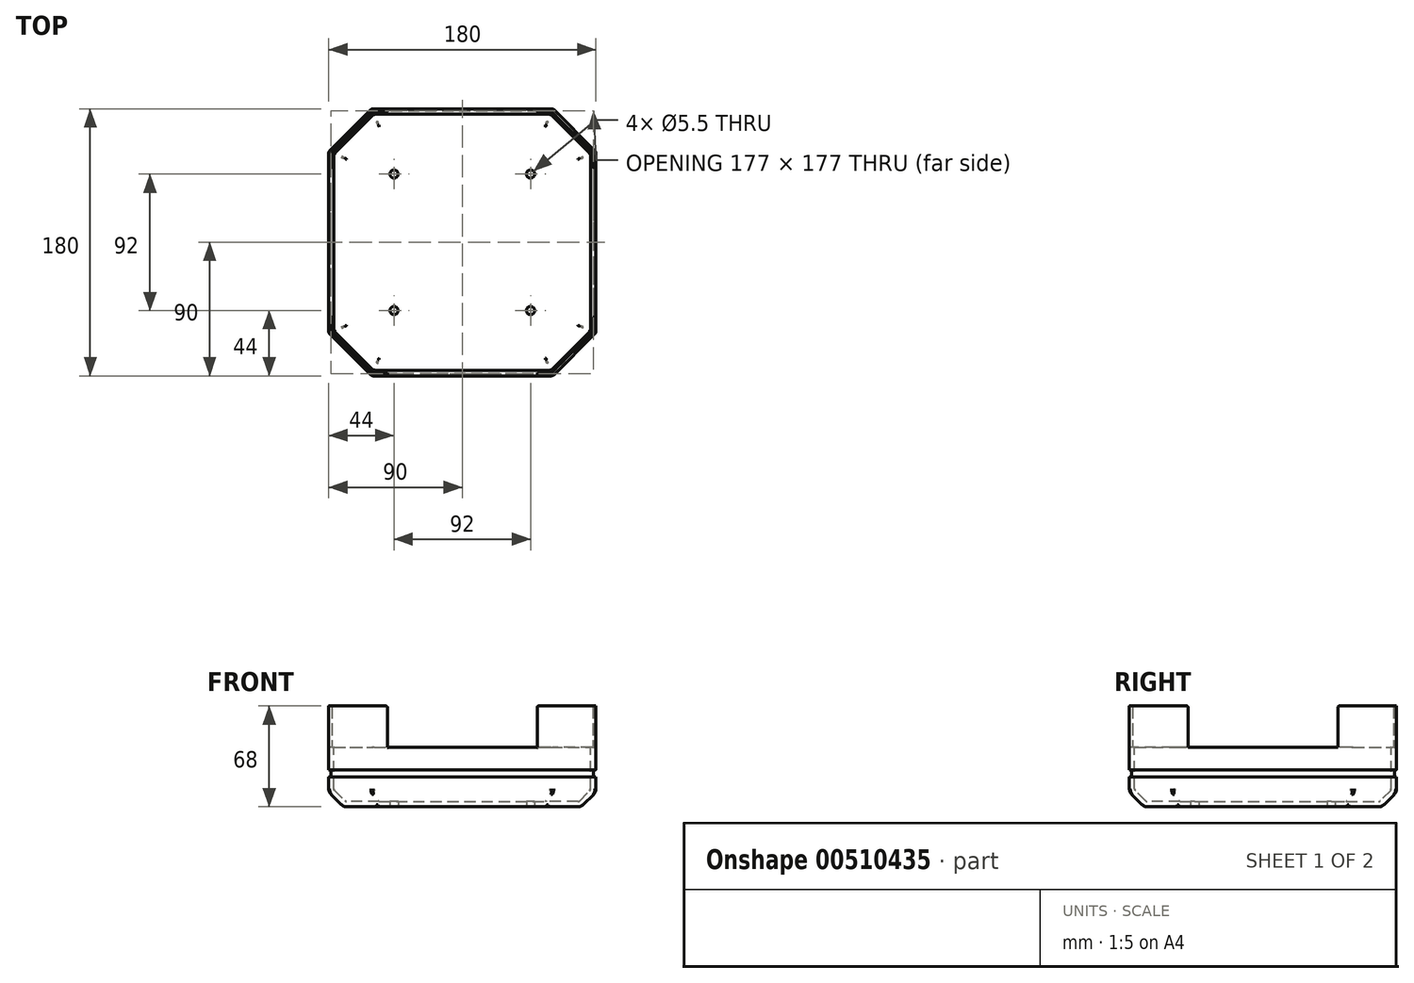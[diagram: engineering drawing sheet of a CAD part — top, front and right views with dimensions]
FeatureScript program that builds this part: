
annotation { "Feature Type Name" : "Feature", "Feature Type Description" : "" }
export const myFeature = defineFeature(function(context is Context, id is Id, definition is map)
    precondition{}
    {
        {
            var Q0;
            Q0=qCreatedBy(makeId("Top.planeOp"),FACE);
            var sketch = newSketch(context, id + "F0", { "sketchPlane" : qUnion([Q0])});
            skLineSegment(sketch, "E0.bottom", {"start": v(-61, 90) * mm, "end": v(61, 90) * mm});
            skLineSegment(sketch, "E0.top", {"start": v(-61, -90) * mm, "end": v(61, -90) * mm});
            skLineSegment(sketch, "E0.left", {"start": v(-90, 61) * mm, "end": v(-90, -61) * mm});
            skLineSegment(sketch, "E0.right", {"start": v(90, 61) * mm, "end": v(90, -61) * mm});
            skLineSegment(sketch, "E1", {"start": v(0, 156.9) * mm, "end": v(0, -146.72) * mm, "construction": true});
            skLineSegment(sketch, "E2", {"start": v(-149.43, 0) * mm, "end": v(169.81, 0) * mm, "construction": true});
            skLineSegment(sketch, "E3", {"start": v(-90, 61) * mm, "end": v(-61, 90) * mm});
            skLineSegment(sketch, "E4", {"start": v(-90, -61) * mm, "end": v(-61, -90) * mm});
            skLineSegment(sketch, "E5", {"start": v(61, -90) * mm, "end": v(90, -61) * mm});
            skLineSegment(sketch, "E6", {"start": v(61, 90) * mm, "end": v(90, 61) * mm});
            skPoint(sketch, "E7.orphan", {"position": v(-90, 90) * mm});
            skPoint(sketch, "E8.orphan", {"position": v(90, 90) * mm});
            skPoint(sketch, "E9.orphan", {"position": v(90, -90) * mm});
            skPoint(sketch, "E10.orphan", {"position": v(-90, -90) * mm});
            skSolve(sketch);
        }
        {
            var Q0;
            Q0=qSketchRegion(id+"F0",true);
            extrude(context, id + "F1", {"entities" : qUnion([Q0]), "depth" : 40 * mm});
        }
        {
            var Q0;
            Q0=makeQuery(id+"F1.opExtrude","CAP_EDGE",EDGE,{"disambiguationData":[OSD([sQuery(id+"F0.wireOp",EDGE,"E0.top")])],"isStart":true});
            var Q1;
            Q1=makeQuery(id+"F1.opExtrude","CAP_EDGE",EDGE,{"disambiguationData":[OSD([sQuery(id+"F0.wireOp",EDGE,"E4")])],"isStart":true});
            var Q2;
            Q2=makeQuery(id+"F1.opExtrude","CAP_EDGE",EDGE,{"disambiguationData":[OSD([sQuery(id+"F0.wireOp",EDGE,"E0.left")])],"isStart":true});
            var Q3;
            Q3=makeQuery(id+"F1.opExtrude","CAP_EDGE",EDGE,{"disambiguationData":[OSD([sQuery(id+"F0.wireOp",EDGE,"E3")])],"isStart":true});
            var Q4;
            Q4=makeQuery(id+"F1.opExtrude","CAP_EDGE",EDGE,{"disambiguationData":[OSD([sQuery(id+"F0.wireOp",EDGE,"E0.bottom")])],"isStart":true});
            var Q5;
            Q5=makeQuery(id+"F1.opExtrude","CAP_EDGE",EDGE,{"disambiguationData":[OSD([sQuery(id+"F0.wireOp",EDGE,"E6")])],"isStart":true});
            var Q6;
            Q6=makeQuery(id+"F1.opExtrude","CAP_EDGE",EDGE,{"disambiguationData":[OSD([sQuery(id+"F0.wireOp",EDGE,"E0.right")])],"isStart":true});
            var Q7;
            Q7=makeQuery(id+"F1.opExtrude","CAP_EDGE",EDGE,{"disambiguationData":[OSD([sQuery(id+"F0.wireOp",EDGE,"E5")])],"isStart":true});
            chamfer(context, id + "F2", {"entities" : qUnion([Q0, Q1, Q2, Q3, Q4, Q5, Q6, Q7]), "chamferType" : ChamferType.TWO_OFFSETS, "width1" : 10 * mm, "oppositeDirection" : true, "width2" : 10 * mm, "tangentPropagation" : true});
        }
        {
            var Q0;
            Q0=makeQuery(id+"F1.opExtrude","CAP_FACE",FACE,{"disambiguationData":[OSD([sQuery(id+"F0.wireOp",EDGE,"E0.bottom"),sQuery(id+"F0.wireOp",EDGE,"E0.top"),sQuery(id+"F0.wireOp",EDGE,"E0.left"),sQuery(id+"F0.wireOp",EDGE,"E0.right"),sQuery(id+"F0.wireOp",EDGE,"E3"),sQuery(id+"F0.wireOp",EDGE,"E4"),sQuery(id+"F0.wireOp",EDGE,"E5"),sQuery(id+"F0.wireOp",EDGE,"E6")])],"isStart":false});
            var sketch = newSketch(context, id + "F3", { "sketchPlane" : qUnion([Q0])});
            skLineSegment(sketch, "E11", {"start": v(90, -61) * mm, "end": v(61, -90) * mm});
            skLineSegment(sketch, "E12.0", {"start": v(88, -60.17) * mm, "end": v(60.17, -88) * mm});
            skLineSegment(sketch, "E13", {"start": v(90, -61) * mm, "end": v(90, -90) * mm, "construction": true});
            skLineSegment(sketch, "E14", {"start": v(90, -90) * mm, "end": v(61, -90) * mm, "construction": true});
            skLineSegment(sketch, "E15", {"start": v(90, -61) * mm, "end": v(90, -50.5) * mm});
            skLineSegment(sketch, "E16", {"start": v(61, -90) * mm, "end": v(50.5, -90) * mm});
            skLineSegment(sketch, "E17.0", {"start": v(60.17, -88) * mm, "end": v(50.5, -88) * mm});
            skLineSegment(sketch, "E18.0", {"start": v(88, -60.17) * mm, "end": v(88, -50.5) * mm});
            skLineSegment(sketch, "E19", {"start": v(88, -50.5) * mm, "end": v(90, -50.5) * mm});
            skLineSegment(sketch, "E20", {"start": v(50.5, -88) * mm, "end": v(50.5, -90) * mm});
            skLineSegment(sketch, "E21", {"start": v(104.54, 0) * mm, "end": v(-130.04, 0) * mm, "construction": true});
            skPoint(sketch, "E21.endSnap0", {"position": v(-90, 0) * mm});
            skLineSegment(sketch, "E22", {"start": v(0, 121.87) * mm, "end": v(0, -139.26) * mm, "construction": true});
            skLineSegment(sketch, "E23.MirrorCS", {"start": v(88, 50.5) * mm, "end": v(90, 50.5) * mm});
            skLineSegment(sketch, "E24.MirrorCS", {"start": v(50.5, 88) * mm, "end": v(50.5, 90) * mm});
            skLineSegment(sketch, "E25.MirrorCS", {"start": v(61, 90) * mm, "end": v(50.5, 90) * mm});
            skLineSegment(sketch, "E26.MirrorCS", {"start": v(60.17, 88) * mm, "end": v(50.5, 88) * mm});
            skLineSegment(sketch, "E27.MirrorCS", {"start": v(88, 60.17) * mm, "end": v(88, 50.5) * mm});
            skLineSegment(sketch, "E28.MirrorCS", {"start": v(90, 61) * mm, "end": v(90, 50.5) * mm});
            skLineSegment(sketch, "E29.MirrorCS", {"start": v(90, 61) * mm, "end": v(61, 90) * mm});
            skLineSegment(sketch, "E30.MirrorCS", {"start": v(88, 60.17) * mm, "end": v(60.17, 88) * mm});
            skLineSegment(sketch, "E31.MirrorCS", {"start": v(90, 90) * mm, "end": v(61, 90) * mm, "construction": true});
            skLineSegment(sketch, "E32.MirrorCS", {"start": v(90, 61) * mm, "end": v(90, 90) * mm, "construction": true});
            skLineSegment(sketch, "E33.MirrorCS", {"start": v(-88, 50.5) * mm, "end": v(-90, 50.5) * mm});
            skLineSegment(sketch, "E34.MirrorCS", {"start": v(-50.5, 88) * mm, "end": v(-50.5, 90) * mm});
            skLineSegment(sketch, "E35.MirrorCS", {"start": v(-88, -50.5) * mm, "end": v(-90, -50.5) * mm});
            skLineSegment(sketch, "E36.MirrorCS", {"start": v(-50.5, -88) * mm, "end": v(-50.5, -90) * mm});
            skLineSegment(sketch, "E37.MirrorCS", {"start": v(-61, -90) * mm, "end": v(-50.5, -90) * mm});
            skLineSegment(sketch, "E38.MirrorCS", {"start": v(-88, 60.17) * mm, "end": v(-88, 50.5) * mm});
            skLineSegment(sketch, "E39.MirrorCS", {"start": v(-61, 90) * mm, "end": v(-50.5, 90) * mm});
            skLineSegment(sketch, "E40.MirrorCS", {"start": v(-88, 60.17) * mm, "end": v(-60.17, 88) * mm});
            skLineSegment(sketch, "E41.MirrorCS", {"start": v(-88, -60.17) * mm, "end": v(-88, -50.5) * mm});
            skLineSegment(sketch, "E42.MirrorCS", {"start": v(-90, 61) * mm, "end": v(-61, 90) * mm});
            skLineSegment(sketch, "E43.MirrorCS", {"start": v(-60.17, 88) * mm, "end": v(-50.5, 88) * mm});
            skLineSegment(sketch, "E44.MirrorCS", {"start": v(-90, 61) * mm, "end": v(-90, 50.5) * mm});
            skLineSegment(sketch, "E45.MirrorCS", {"start": v(-90, -61) * mm, "end": v(-90, -50.5) * mm});
            skLineSegment(sketch, "E46.MirrorCS", {"start": v(-60.17, -88) * mm, "end": v(-50.5, -88) * mm});
            skLineSegment(sketch, "E47.MirrorCS", {"start": v(-90, 90) * mm, "end": v(-61, 90) * mm, "construction": true});
            skLineSegment(sketch, "E48.MirrorCS", {"start": v(-90, 61) * mm, "end": v(-90, 90) * mm, "construction": true});
            skLineSegment(sketch, "E49.MirrorCS", {"start": v(-90, -61) * mm, "end": v(-61, -90) * mm});
            skLineSegment(sketch, "E50.MirrorCS", {"start": v(-90, -61) * mm, "end": v(-90, -90) * mm, "construction": true});
            skLineSegment(sketch, "E51.MirrorCS", {"start": v(-90, -90) * mm, "end": v(-61, -90) * mm, "construction": true});
            skLineSegment(sketch, "E52.MirrorCS", {"start": v(-88, -60.17) * mm, "end": v(-60.17, -88) * mm});
            skSolve(sketch);
        }
        {
            var Q0;
            Q0=qSketchRegion(id+"F3",true);
            extrude(context, id + "F4", {"entities" : qUnion([Q0]), "operationType" : NewBodyOperationType.ADD, "depth" : 28 * mm});
        }
        {
            var Q0;
            {var subQ0=sQuery(id+"F0.wireOp",EDGE,"E6");Q0=makeQuery(id+"F2.opChamfer","BLEND_EDGE",EDGE,{"blendedFrom":[makeQuery(id+"F1.opExtrude","CAP_EDGE",EDGE,{"disambiguationData":[OSD([subQ0])],"isStart":true}),makeQuery(id+"F1.opExtrude","SWEPT_FACE",FACE,{"disambiguationData":[OSD([subQ0])]})],"blendedInto":[makeQuery(id+"F1.opExtrude","SWEPT_FACE",FACE,{"disambiguationData":[OSD([subQ0])]})]});}
            var Q1;
            {var subQ0=sQuery(id+"F0.wireOp",EDGE,"E0.right");Q1=makeQuery(id+"F2.opChamfer","BLEND_EDGE",EDGE,{"blendedFrom":[makeQuery(id+"F1.opExtrude","CAP_EDGE",EDGE,{"disambiguationData":[OSD([subQ0])],"isStart":true}),makeQuery(id+"F1.opExtrude","SWEPT_FACE",FACE,{"disambiguationData":[OSD([subQ0])]})],"blendedInto":[makeQuery(id+"F1.opExtrude","SWEPT_FACE",FACE,{"disambiguationData":[OSD([subQ0])]})]});}
            var Q2;
            {var subQ0=sQuery(id+"F0.wireOp",EDGE,"E5");Q2=makeQuery(id+"F2.opChamfer","BLEND_EDGE",EDGE,{"blendedFrom":[makeQuery(id+"F1.opExtrude","CAP_EDGE",EDGE,{"disambiguationData":[OSD([subQ0])],"isStart":true}),makeQuery(id+"F1.opExtrude","SWEPT_FACE",FACE,{"disambiguationData":[OSD([subQ0])]})],"blendedInto":[makeQuery(id+"F1.opExtrude","SWEPT_FACE",FACE,{"disambiguationData":[OSD([subQ0])]})]});}
            var Q3;
            {var subQ0=sQuery(id+"F0.wireOp",EDGE,"E0.top");Q3=makeQuery(id+"F2.opChamfer","BLEND_EDGE",EDGE,{"blendedFrom":[makeQuery(id+"F1.opExtrude","CAP_EDGE",EDGE,{"disambiguationData":[OSD([subQ0])],"isStart":true}),makeQuery(id+"F1.opExtrude","SWEPT_FACE",FACE,{"disambiguationData":[OSD([subQ0])]})],"blendedInto":[makeQuery(id+"F1.opExtrude","SWEPT_FACE",FACE,{"disambiguationData":[OSD([subQ0])]})]});}
            var Q4;
            {var subQ0=sQuery(id+"F0.wireOp",EDGE,"E4");Q4=makeQuery(id+"F2.opChamfer","BLEND_EDGE",EDGE,{"blendedFrom":[makeQuery(id+"F1.opExtrude","CAP_EDGE",EDGE,{"disambiguationData":[OSD([subQ0])],"isStart":true}),makeQuery(id+"F1.opExtrude","SWEPT_FACE",FACE,{"disambiguationData":[OSD([subQ0])]})],"blendedInto":[makeQuery(id+"F1.opExtrude","SWEPT_FACE",FACE,{"disambiguationData":[OSD([subQ0])]})]});}
            var Q5;
            {var subQ0=sQuery(id+"F0.wireOp",EDGE,"E0.left");Q5=makeQuery(id+"F2.opChamfer","BLEND_EDGE",EDGE,{"blendedFrom":[makeQuery(id+"F1.opExtrude","CAP_EDGE",EDGE,{"disambiguationData":[OSD([subQ0])],"isStart":true}),makeQuery(id+"F1.opExtrude","SWEPT_FACE",FACE,{"disambiguationData":[OSD([subQ0])]})],"blendedInto":[makeQuery(id+"F1.opExtrude","SWEPT_FACE",FACE,{"disambiguationData":[OSD([subQ0])]})]});}
            var Q6;
            {var subQ0=sQuery(id+"F0.wireOp",EDGE,"E3");Q6=makeQuery(id+"F2.opChamfer","BLEND_EDGE",EDGE,{"blendedFrom":[makeQuery(id+"F1.opExtrude","CAP_EDGE",EDGE,{"disambiguationData":[OSD([subQ0])],"isStart":true}),makeQuery(id+"F1.opExtrude","SWEPT_FACE",FACE,{"disambiguationData":[OSD([subQ0])]})],"blendedInto":[makeQuery(id+"F1.opExtrude","SWEPT_FACE",FACE,{"disambiguationData":[OSD([subQ0])]})]});}
            var Q7;
            {var subQ0=sQuery(id+"F0.wireOp",EDGE,"E0.bottom");Q7=makeQuery(id+"F2.opChamfer","BLEND_EDGE",EDGE,{"blendedFrom":[makeQuery(id+"F1.opExtrude","CAP_EDGE",EDGE,{"disambiguationData":[OSD([subQ0])],"isStart":true}),makeQuery(id+"F1.opExtrude","SWEPT_FACE",FACE,{"disambiguationData":[OSD([subQ0])]})],"blendedInto":[makeQuery(id+"F1.opExtrude","SWEPT_FACE",FACE,{"disambiguationData":[OSD([subQ0])]})]});}
            fillet(context, id + "F5", {"entities" : qUnion([Q0, Q1, Q2, Q3, Q4, Q5, Q6, Q7]), "radius" : 5 * mm, "tangentPropagation" : true, "allowEdgeOverflow" : false});
        }
        {
            var Q0;
            Q0=makeQuery(id+"F4.boolean.opBoolean","MERGE",EDGE,{"derivedFrom":[makeQuery(id+"F1.opExtrude","SWEPT_EDGE",EDGE,{"disambiguationData":[OSD([sQuery(id+"F0.wireOp",EDGE,"E0.bottom"),sQuery(id+"F0.wireOp",EDGE,"E6")])]}),makeQuery(id+"F4.opExtrude","SWEPT_EDGE",EDGE,{"disambiguationData":[OSD([sQuery(id+"F3.wireOp",EDGE,"E25.MirrorCS"),sQuery(id+"F3.wireOp",EDGE,"E29.MirrorCS")])]})]});
            var Q1;
            Q1=makeQuery(id+"F4.boolean.opBoolean","MERGE",EDGE,{"derivedFrom":[makeQuery(id+"F1.opExtrude","SWEPT_EDGE",EDGE,{"disambiguationData":[OSD([sQuery(id+"F0.wireOp",EDGE,"E0.right"),sQuery(id+"F0.wireOp",EDGE,"E6")])]}),makeQuery(id+"F4.opExtrude","SWEPT_EDGE",EDGE,{"disambiguationData":[OSD([sQuery(id+"F3.wireOp",EDGE,"E28.MirrorCS"),sQuery(id+"F3.wireOp",EDGE,"E29.MirrorCS")])]})]});
            var Q2;
            Q2=makeQuery(id+"F4.boolean.opBoolean","MERGE",EDGE,{"derivedFrom":[makeQuery(id+"F1.opExtrude","SWEPT_EDGE",EDGE,{"disambiguationData":[OSD([sQuery(id+"F0.wireOp",EDGE,"E0.bottom"),sQuery(id+"F0.wireOp",EDGE,"E3")])]}),makeQuery(id+"F4.opExtrude","SWEPT_EDGE",EDGE,{"disambiguationData":[OSD([sQuery(id+"F3.wireOp",EDGE,"E39.MirrorCS"),sQuery(id+"F3.wireOp",EDGE,"E42.MirrorCS")])]})]});
            var Q3;
            Q3=makeQuery(id+"F4.boolean.opBoolean","MERGE",EDGE,{"derivedFrom":[makeQuery(id+"F1.opExtrude","SWEPT_EDGE",EDGE,{"disambiguationData":[OSD([sQuery(id+"F0.wireOp",EDGE,"E0.right"),sQuery(id+"F0.wireOp",EDGE,"E5")])]}),makeQuery(id+"F4.opExtrude","SWEPT_EDGE",EDGE,{"disambiguationData":[OSD([sQuery(id+"F3.wireOp",EDGE,"E11"),sQuery(id+"F3.wireOp",EDGE,"E15")])]})]});
            var Q4;
            Q4=makeQuery(id+"F2.opChamfer","BLEND_EDGE",EDGE,{"blendedFrom":[makeQuery(id+"F1.opExtrude","CAP_EDGE",EDGE,{"disambiguationData":[OSD([sQuery(id+"F0.wireOp",EDGE,"E0.top")])],"isStart":true}),makeQuery(id+"F1.opExtrude","CAP_EDGE",EDGE,{"disambiguationData":[OSD([sQuery(id+"F0.wireOp",EDGE,"E5")])],"isStart":true})],"blendedInto":[]});
            var Q5;
            Q5=makeQuery(id+"F2.opChamfer","BLEND_EDGE",EDGE,{"blendedFrom":[makeQuery(id+"F1.opExtrude","CAP_EDGE",EDGE,{"disambiguationData":[OSD([sQuery(id+"F0.wireOp",EDGE,"E0.top")])],"isStart":true}),makeQuery(id+"F1.opExtrude","CAP_EDGE",EDGE,{"disambiguationData":[OSD([sQuery(id+"F0.wireOp",EDGE,"E4")])],"isStart":true})],"blendedInto":[]});
            var Q6;
            Q6=makeQuery(id+"F2.opChamfer","BLEND_EDGE",EDGE,{"blendedFrom":[makeQuery(id+"F1.opExtrude","CAP_EDGE",EDGE,{"disambiguationData":[OSD([sQuery(id+"F0.wireOp",EDGE,"E0.left")])],"isStart":true}),makeQuery(id+"F1.opExtrude","CAP_EDGE",EDGE,{"disambiguationData":[OSD([sQuery(id+"F0.wireOp",EDGE,"E4")])],"isStart":true})],"blendedInto":[]});
            var Q7;
            Q7=makeQuery(id+"F2.opChamfer","BLEND_EDGE",EDGE,{"blendedFrom":[makeQuery(id+"F1.opExtrude","CAP_EDGE",EDGE,{"disambiguationData":[OSD([sQuery(id+"F0.wireOp",EDGE,"E0.left")])],"isStart":true}),makeQuery(id+"F1.opExtrude","CAP_EDGE",EDGE,{"disambiguationData":[OSD([sQuery(id+"F0.wireOp",EDGE,"E3")])],"isStart":true})],"blendedInto":[]});
            fillet(context, id + "F6", {"entities" : qUnion([Q0, Q1, Q2, Q3, Q4, Q5, Q6, Q7]), "radius" : 2 * mm, "tangentPropagation" : true, "allowEdgeOverflow" : false});
        }
        {
            var Q0;
            {var subQ0=sQuery(id+"F0.wireOp",EDGE,"E0.left");Q0=makeQuery(id+"F2.opChamfer","BLEND_EDGE",EDGE,{"blendedFrom":[makeQuery(id+"F1.opExtrude","CAP_EDGE",EDGE,{"disambiguationData":[OSD([subQ0])],"isStart":true}),makeQuery(id+"F1.opExtrude","CAP_FACE",FACE,{"disambiguationData":[OSD([sQuery(id+"F0.wireOp",EDGE,"E0.bottom"),sQuery(id+"F0.wireOp",EDGE,"E0.top"),subQ0,sQuery(id+"F0.wireOp",EDGE,"E0.right"),sQuery(id+"F0.wireOp",EDGE,"E3"),sQuery(id+"F0.wireOp",EDGE,"E4"),sQuery(id+"F0.wireOp",EDGE,"E5"),sQuery(id+"F0.wireOp",EDGE,"E6")])],"isStart":true})],"blendedInto":[makeQuery(id+"F1.opExtrude","CAP_FACE",FACE,{"disambiguationData":[OSD([sQuery(id+"F0.wireOp",EDGE,"E0.bottom"),sQuery(id+"F0.wireOp",EDGE,"E0.top"),subQ0,sQuery(id+"F0.wireOp",EDGE,"E0.right"),sQuery(id+"F0.wireOp",EDGE,"E3"),sQuery(id+"F0.wireOp",EDGE,"E4"),sQuery(id+"F0.wireOp",EDGE,"E5"),sQuery(id+"F0.wireOp",EDGE,"E6")])],"isStart":true})]});}
            fillet(context, id + "F7", {"entities" : qUnion([Q0]), "radius" : 5 * mm, "tangentPropagation" : true, "allowEdgeOverflow" : false});
        }
        {
            var Q0;
            Q0=makeQuery(id+"F1.opExtrude","CAP_FACE",FACE,{"disambiguationData":[OSD([sQuery(id+"F0.wireOp",EDGE,"E0.bottom"),sQuery(id+"F0.wireOp",EDGE,"E0.top"),sQuery(id+"F0.wireOp",EDGE,"E0.left"),sQuery(id+"F0.wireOp",EDGE,"E0.right"),sQuery(id+"F0.wireOp",EDGE,"E3"),sQuery(id+"F0.wireOp",EDGE,"E4"),sQuery(id+"F0.wireOp",EDGE,"E5"),sQuery(id+"F0.wireOp",EDGE,"E6")])],"isStart":false});
            shell(context, id + "F8", {"entities" : qUnion([Q0]), "thickness" : 3.5 * mm});
        }
        {
            var Q0;
            Q0=qCreatedBy(makeId("Front.planeOp"),FACE);
            var sketch = newSketch(context, id + "F9", { "sketchPlane" : qUnion([Q0])});
            skLineSegment(sketch, "E53.bottom", {"start": v(124, 20) * mm, "end": v(-129.94, 20) * mm});
            skLineSegment(sketch, "E53.top", {"start": v(124, 25) * mm, "end": v(-129.94, 25) * mm});
            skLineSegment(sketch, "E53.left", {"start": v(124, 20) * mm, "end": v(124, 25) * mm});
            skLineSegment(sketch, "E53.right", {"start": v(-129.94, 20) * mm, "end": v(-129.94, 25) * mm});
            skSolve(sketch);
        }
        {
            var Q0;
            Q0=qSketchRegion(id+"F9",true);
            extrude(context, id + "F10", {"entities" : qUnion([Q0]), "operationType" : NewBodyOperationType.REMOVE, "oppositeDirection" : true, "depth" : 180 * mm, "symmetric" : true});
        }
        {
            var Q0;
            Q0=makeQuery(id+"F10.boolean.opBoolean","COPY",FACE,{"derivedFrom":makeQuery(id+"F10.opExtrude","SWEPT_FACE",FACE,{"disambiguationData":[OSD([sQuery(id+"F9.wireOp",EDGE,"E53.bottom")])]})});
            var sketch = newSketch(context, id + "F11", { "sketchPlane" : qUnion([Q0])});
            skLineSegment(sketch, "E54.0", {"start": v(-60.38, -88.5) * mm, "end": v(60.38, -88.5) * mm});
            skLineSegment(sketch, "E54.1", {"start": v(-88.5, -60.38) * mm, "end": v(-60.38, -88.5) * mm});
            skLineSegment(sketch, "E54.2", {"start": v(60.38, -88.5) * mm, "end": v(88.5, -60.38) * mm});
            skLineSegment(sketch, "E54.3", {"start": v(-88.5, 60.38) * mm, "end": v(-88.5, -60.38) * mm});
            skLineSegment(sketch, "E54.4", {"start": v(88.5, -60.38) * mm, "end": v(88.5, 60.38) * mm});
            skLineSegment(sketch, "E54.5", {"start": v(88.5, 60.38) * mm, "end": v(60.38, 88.5) * mm});
            skLineSegment(sketch, "E54.6", {"start": v(60.38, 88.5) * mm, "end": v(-60.38, 88.5) * mm});
            skLineSegment(sketch, "E54.7", {"start": v(-60.38, 88.5) * mm, "end": v(-88.5, 60.38) * mm});
            skLineSegment(sketch, "E55.0", {"start": v(-59.55, 86.5) * mm, "end": v(-59.55, 86.5) * mm});
            skLineSegment(sketch, "E55.2", {"start": v(-86.5, 59.55) * mm, "end": v(-86.5, -59.55) * mm});
            skLineSegment(sketch, "E55.4", {"start": v(-59.55, 86.5) * mm, "end": v(59.55, 86.5) * mm});
            skLineSegment(sketch, "E55.6", {"start": v(59.55, 86.5) * mm, "end": v(59.55, 86.5) * mm});
            skLineSegment(sketch, "E55.8", {"start": v(86.5, 59.55) * mm, "end": v(86.5, -59.55) * mm});
            skLineSegment(sketch, "E55.10", {"start": v(59.55, -86.5) * mm, "end": v(59.55, -86.5) * mm});
            skLineSegment(sketch, "E55.12", {"start": v(-59.55, -86.5) * mm, "end": v(59.55, -86.5) * mm});
            skLineSegment(sketch, "E55.14", {"start": v(-59.55, -86.5) * mm, "end": v(-59.55, -86.5) * mm});
            skLineSegment(sketch, "E56", {"start": v(86.5, 59.55) * mm, "end": v(59.55, 86.5) * mm});
            skLineSegment(sketch, "E57", {"start": v(-59.55, 86.5) * mm, "end": v(-86.5, 59.55) * mm});
            skLineSegment(sketch, "E58", {"start": v(-59.55, -86.5) * mm, "end": v(-86.5, -59.55) * mm});
            skLineSegment(sketch, "E59", {"start": v(86.5, -59.55) * mm, "end": v(59.55, -86.5) * mm});
            skSolve(sketch);
        }
        {
            var Q0;
            Q0=qSketchRegion(id+"F11",true);
            extrude(context, id + "F12", {"entities" : qUnion([Q0]), "operationType" : NewBodyOperationType.ADD, "depth" : 10 * mm});
        }
        {
            var Q0;
            {var subQ0=sQuery(id+"F11.wireOp",EDGE,"E54.7");var subQ1=sQuery(id+"F11.wireOp",EDGE,"E54.3");Q0=makeQuery(id+"F12.boolean.opBoolean","SPLIT",EDGE,{"disambiguationData":[TD([makeQuery(id+"F10.boolean.opBoolean","COPY",FACE,{"derivedFrom":makeQuery(id+"F10.opExtrude","SWEPT_FACE",FACE,{"disambiguationData":[OSD([sQuery(id+"F9.wireOp",EDGE,"E53.bottom")])]})})])],"derivedFrom":makeQuery(id+"F12.opExtrude","SWEPT_EDGE",EDGE,{"disambiguationData":[OSD([subQ1,subQ0])]})});}
            var Q1;
            {var subQ0=sQuery(id+"F11.wireOp",EDGE,"E54.7");var subQ1=sQuery(id+"F11.wireOp",EDGE,"E54.6");Q1=makeQuery(id+"F12.boolean.opBoolean","SPLIT",EDGE,{"disambiguationData":[TD([makeQuery(id+"F10.boolean.opBoolean","COPY",FACE,{"derivedFrom":makeQuery(id+"F10.opExtrude","SWEPT_FACE",FACE,{"disambiguationData":[OSD([sQuery(id+"F9.wireOp",EDGE,"E53.bottom")])]})})])],"derivedFrom":makeQuery(id+"F12.opExtrude","SWEPT_EDGE",EDGE,{"disambiguationData":[OSD([subQ1,subQ0])]})});}
            var Q2;
            {var subQ0=sQuery(id+"F11.wireOp",EDGE,"E54.5");var subQ1=sQuery(id+"F11.wireOp",EDGE,"E54.6");Q2=makeQuery(id+"F12.boolean.opBoolean","SPLIT",EDGE,{"disambiguationData":[TD([makeQuery(id+"F10.boolean.opBoolean","COPY",FACE,{"derivedFrom":makeQuery(id+"F10.opExtrude","SWEPT_FACE",FACE,{"disambiguationData":[OSD([sQuery(id+"F9.wireOp",EDGE,"E53.bottom")])]})})])],"derivedFrom":makeQuery(id+"F12.opExtrude","SWEPT_EDGE",EDGE,{"disambiguationData":[OSD([subQ0,subQ1])]})});}
            var Q3;
            {var subQ0=sQuery(id+"F11.wireOp",EDGE,"E54.5");var subQ1=sQuery(id+"F11.wireOp",EDGE,"E54.6");Q3=makeQuery(id+"F12.boolean.opBoolean","SPLIT",EDGE,{"disambiguationData":[TD([makeQuery(id+"F10.boolean.opBoolean","COPY",FACE,{"derivedFrom":makeQuery(id+"F10.opExtrude","SWEPT_FACE",FACE,{"disambiguationData":[OSD([sQuery(id+"F9.wireOp",EDGE,"Me13D1SK-nVIm-EUZ4-u9ei-o20qw3bNrjn4.bottom")])]})})])],"derivedFrom":makeQuery(id+"F12.opExtrude","SWEPT_EDGE",EDGE,{"disambiguationData":[OSD([subQ0,subQ1])]})});}
            var Q4;
            {var subQ0=sQuery(id+"F11.wireOp",EDGE,"E54.6");var subQ1=sQuery(id+"F11.wireOp",EDGE,"E54.7");Q4=makeQuery(id+"F12.boolean.opBoolean","SPLIT",EDGE,{"disambiguationData":[TD([makeQuery(id+"F10.boolean.opBoolean","COPY",FACE,{"derivedFrom":makeQuery(id+"F10.opExtrude","SWEPT_FACE",FACE,{"disambiguationData":[OSD([sQuery(id+"F9.wireOp",EDGE,"Me13D1SK-nVIm-EUZ4-u9ei-o20qw3bNrjn4.bottom")])]})})])],"derivedFrom":makeQuery(id+"F12.opExtrude","SWEPT_EDGE",EDGE,{"disambiguationData":[OSD([subQ0,subQ1])]})});}
            var Q5;
            {var subQ0=sQuery(id+"F11.wireOp",EDGE,"E54.3");var subQ1=sQuery(id+"F11.wireOp",EDGE,"E54.7");Q5=makeQuery(id+"F12.boolean.opBoolean","SPLIT",EDGE,{"disambiguationData":[TD([makeQuery(id+"F10.boolean.opBoolean","COPY",FACE,{"derivedFrom":makeQuery(id+"F10.opExtrude","SWEPT_FACE",FACE,{"disambiguationData":[OSD([sQuery(id+"F9.wireOp",EDGE,"Me13D1SK-nVIm-EUZ4-u9ei-o20qw3bNrjn4.bottom")])]})})])],"derivedFrom":makeQuery(id+"F12.opExtrude","SWEPT_EDGE",EDGE,{"disambiguationData":[OSD([subQ0,subQ1])]})});}
            var Q6;
            {var subQ0=sQuery(id+"F11.wireOp",EDGE,"E54.5");var subQ1=sQuery(id+"F11.wireOp",EDGE,"E54.4");Q6=makeQuery(id+"F12.boolean.opBoolean","SPLIT",EDGE,{"disambiguationData":[TD([makeQuery(id+"F10.boolean.opBoolean","COPY",FACE,{"derivedFrom":makeQuery(id+"F10.opExtrude","SWEPT_FACE",FACE,{"disambiguationData":[OSD([sQuery(id+"F9.wireOp",EDGE,"Me13D1SK-nVIm-EUZ4-u9ei-o20qw3bNrjn4.bottom")])]})})])],"derivedFrom":makeQuery(id+"F12.opExtrude","SWEPT_EDGE",EDGE,{"disambiguationData":[OSD([subQ1,subQ0])]})});}
            var Q7;
            {var subQ0=sQuery(id+"F11.wireOp",EDGE,"E54.4");var subQ1=sQuery(id+"F11.wireOp",EDGE,"E54.5");Q7=makeQuery(id+"F12.boolean.opBoolean","SPLIT",EDGE,{"disambiguationData":[TD([makeQuery(id+"F10.boolean.opBoolean","COPY",FACE,{"derivedFrom":makeQuery(id+"F10.opExtrude","SWEPT_FACE",FACE,{"disambiguationData":[OSD([sQuery(id+"F9.wireOp",EDGE,"E53.bottom")])]})})])],"derivedFrom":makeQuery(id+"F12.opExtrude","SWEPT_EDGE",EDGE,{"disambiguationData":[OSD([subQ0,subQ1])]})});}
            var Q8;
            {var subQ0=sQuery(id+"F11.wireOp",EDGE,"E54.2");var subQ1=sQuery(id+"F11.wireOp",EDGE,"E54.4");Q8=makeQuery(id+"F12.boolean.opBoolean","SPLIT",EDGE,{"disambiguationData":[TD([makeQuery(id+"F10.boolean.opBoolean","COPY",FACE,{"derivedFrom":makeQuery(id+"F10.opExtrude","SWEPT_FACE",FACE,{"disambiguationData":[OSD([sQuery(id+"F9.wireOp",EDGE,"E53.bottom")])]})})])],"derivedFrom":makeQuery(id+"F12.opExtrude","SWEPT_EDGE",EDGE,{"disambiguationData":[OSD([subQ0,subQ1])]})});}
            var Q9;
            {var subQ0=sQuery(id+"F11.wireOp",EDGE,"E54.2");var subQ1=sQuery(id+"F11.wireOp",EDGE,"E54.0");Q9=makeQuery(id+"F12.boolean.opBoolean","SPLIT",EDGE,{"disambiguationData":[TD([makeQuery(id+"F10.boolean.opBoolean","COPY",FACE,{"derivedFrom":makeQuery(id+"F10.opExtrude","SWEPT_FACE",FACE,{"disambiguationData":[OSD([sQuery(id+"F9.wireOp",EDGE,"E53.bottom")])]})})])],"derivedFrom":makeQuery(id+"F12.opExtrude","SWEPT_EDGE",EDGE,{"disambiguationData":[OSD([subQ1,subQ0])]})});}
            var Q10;
            {var subQ0=sQuery(id+"F11.wireOp",EDGE,"E54.2");var subQ1=sQuery(id+"F11.wireOp",EDGE,"E54.4");Q10=makeQuery(id+"F12.boolean.opBoolean","SPLIT",EDGE,{"disambiguationData":[TD([makeQuery(id+"F10.boolean.opBoolean","COPY",FACE,{"derivedFrom":makeQuery(id+"F10.opExtrude","SWEPT_FACE",FACE,{"disambiguationData":[OSD([sQuery(id+"F9.wireOp",EDGE,"Me13D1SK-nVIm-EUZ4-u9ei-o20qw3bNrjn4.bottom")])]})})])],"derivedFrom":makeQuery(id+"F12.opExtrude","SWEPT_EDGE",EDGE,{"disambiguationData":[OSD([subQ0,subQ1])]})});}
            var Q11;
            {var subQ0=sQuery(id+"F11.wireOp",EDGE,"E54.0");var subQ1=sQuery(id+"F11.wireOp",EDGE,"E54.2");Q11=makeQuery(id+"F12.boolean.opBoolean","SPLIT",EDGE,{"disambiguationData":[TD([makeQuery(id+"F10.boolean.opBoolean","COPY",FACE,{"derivedFrom":makeQuery(id+"F10.opExtrude","SWEPT_FACE",FACE,{"disambiguationData":[OSD([sQuery(id+"F9.wireOp",EDGE,"Me13D1SK-nVIm-EUZ4-u9ei-o20qw3bNrjn4.bottom")])]})})])],"derivedFrom":makeQuery(id+"F12.opExtrude","SWEPT_EDGE",EDGE,{"disambiguationData":[OSD([subQ0,subQ1])]})});}
            var Q12;
            {var subQ0=sQuery(id+"F11.wireOp",EDGE,"E54.0");var subQ1=sQuery(id+"F11.wireOp",EDGE,"E54.1");Q12=makeQuery(id+"F12.boolean.opBoolean","SPLIT",EDGE,{"disambiguationData":[TD([makeQuery(id+"F10.boolean.opBoolean","COPY",FACE,{"derivedFrom":makeQuery(id+"F10.opExtrude","SWEPT_FACE",FACE,{"disambiguationData":[OSD([sQuery(id+"F9.wireOp",EDGE,"E53.bottom")])]})})])],"derivedFrom":makeQuery(id+"F12.opExtrude","SWEPT_EDGE",EDGE,{"disambiguationData":[OSD([subQ0,subQ1])]})});}
            var Q13;
            {var subQ0=sQuery(id+"F11.wireOp",EDGE,"E54.3");var subQ1=sQuery(id+"F11.wireOp",EDGE,"E54.1");Q13=makeQuery(id+"F12.boolean.opBoolean","SPLIT",EDGE,{"disambiguationData":[TD([makeQuery(id+"F10.boolean.opBoolean","COPY",FACE,{"derivedFrom":makeQuery(id+"F10.opExtrude","SWEPT_FACE",FACE,{"disambiguationData":[OSD([sQuery(id+"F9.wireOp",EDGE,"E53.bottom")])]})})])],"derivedFrom":makeQuery(id+"F12.opExtrude","SWEPT_EDGE",EDGE,{"disambiguationData":[OSD([subQ1,subQ0])]})});}
            var Q14;
            {var subQ0=sQuery(id+"F11.wireOp",EDGE,"E54.1");var subQ1=sQuery(id+"F11.wireOp",EDGE,"E54.0");Q14=makeQuery(id+"F12.boolean.opBoolean","SPLIT",EDGE,{"disambiguationData":[TD([makeQuery(id+"F10.boolean.opBoolean","COPY",FACE,{"derivedFrom":makeQuery(id+"F10.opExtrude","SWEPT_FACE",FACE,{"disambiguationData":[OSD([sQuery(id+"F9.wireOp",EDGE,"Me13D1SK-nVIm-EUZ4-u9ei-o20qw3bNrjn4.bottom")])]})})])],"derivedFrom":makeQuery(id+"F12.opExtrude","SWEPT_EDGE",EDGE,{"disambiguationData":[OSD([subQ1,subQ0])]})});}
            var Q15;
            {var subQ0=sQuery(id+"F11.wireOp",EDGE,"E54.1");var subQ1=sQuery(id+"F11.wireOp",EDGE,"E54.3");Q15=makeQuery(id+"F12.boolean.opBoolean","SPLIT",EDGE,{"disambiguationData":[TD([makeQuery(id+"F10.boolean.opBoolean","COPY",FACE,{"derivedFrom":makeQuery(id+"F10.opExtrude","SWEPT_FACE",FACE,{"disambiguationData":[OSD([sQuery(id+"F9.wireOp",EDGE,"Me13D1SK-nVIm-EUZ4-u9ei-o20qw3bNrjn4.bottom")])]})})])],"derivedFrom":makeQuery(id+"F12.opExtrude","SWEPT_EDGE",EDGE,{"disambiguationData":[OSD([subQ0,subQ1])]})});}
            fillet(context, id + "F13", {"entities" : qUnion([Q0, Q1, Q2, Q3, Q4, Q5, Q6, Q7, Q8, Q9, Q10, Q11, Q12, Q13, Q14, Q15]), "radius" : 2 * mm, "tangentPropagation" : true, "allowEdgeOverflow" : false});
        }
        {
            var Q0;
            Q0=makeQuery(id+"F1.opExtrude","CAP_FACE",FACE,{"disambiguationData":[OSD([sQuery(id+"F0.wireOp",EDGE,"E0.bottom"),sQuery(id+"F0.wireOp",EDGE,"E0.top"),sQuery(id+"F0.wireOp",EDGE,"E0.left"),sQuery(id+"F0.wireOp",EDGE,"E0.right"),sQuery(id+"F0.wireOp",EDGE,"E3"),sQuery(id+"F0.wireOp",EDGE,"E4"),sQuery(id+"F0.wireOp",EDGE,"E5"),sQuery(id+"F0.wireOp",EDGE,"E6")])],"isStart":true});
            var sketch = newSketch(context, id + "F14", { "sketchPlane" : qUnion([Q0])});
            skLineSegment(sketch, "E60", {"start": v(0, 77.93) * mm, "end": v(0, -77.93) * mm, "construction": true});
            skLineSegment(sketch, "E61", {"start": v(-77.93, 0) * mm, "end": v(77.93, 0) * mm, "construction": true});
            skLineSegment(sketch, "E62", {"start": v(-66.96, -66.96) * mm, "end": v(66.96, 66.96) * mm, "construction": true});
            skLineSegment(sketch, "E63", {"start": v(-66.96, 66.96) * mm, "end": v(66.96, -66.96) * mm, "construction": true});
            skCircle(sketch, "E64", {"center": v(-46, -46) * mm, "radius": 2.75 * mm});
            skCircle(sketch, "E65", {"center": v(-46, 46) * mm, "radius": 2.75 * mm});
            skCircle(sketch, "E66", {"center": v(46, 46) * mm, "radius": 2.75 * mm});
            skCircle(sketch, "E67", {"center": v(46, -46) * mm, "radius": 2.75 * mm});
            skSolve(sketch);
        }
        {
            var Q0;
            Q0=qSketchRegion(id+"F14",true);
            extrude(context, id + "F15", {"entities" : qUnion([Q0]), "operationType" : NewBodyOperationType.REMOVE, "oppositeDirection" : true, "depth" : 25 * mm});
        }
        {
            var Q0;
            Q0=makeQuery(id+"F4.opExtrude","SWEPT_EDGE",EDGE,{"disambiguationData":[OSD([sQuery(id+"F3.wireOp",EDGE,"E41.MirrorCS"),sQuery(id+"F3.wireOp",EDGE,"E52.MirrorCS")])]});
            var Q1;
            Q1=makeQuery(id+"F4.opExtrude","SWEPT_EDGE",EDGE,{"disambiguationData":[OSD([sQuery(id+"F3.wireOp",EDGE,"E46.MirrorCS"),sQuery(id+"F3.wireOp",EDGE,"E52.MirrorCS")])]});
            var Q2;
            Q2=makeQuery(id+"F4.opExtrude","SWEPT_EDGE",EDGE,{"disambiguationData":[OSD([sQuery(id+"F3.wireOp",EDGE,"E12.0"),sQuery(id+"F3.wireOp",EDGE,"E18.0")])]});
            var Q3;
            Q3=makeQuery(id+"F4.opExtrude","SWEPT_EDGE",EDGE,{"disambiguationData":[OSD([sQuery(id+"F3.wireOp",EDGE,"E12.0"),sQuery(id+"F3.wireOp",EDGE,"E17.0")])]});
            var Q4;
            Q4=makeQuery(id+"F4.opExtrude","SWEPT_EDGE",EDGE,{"disambiguationData":[OSD([sQuery(id+"F3.wireOp",EDGE,"E27.MirrorCS"),sQuery(id+"F3.wireOp",EDGE,"E30.MirrorCS")])]});
            var Q5;
            Q5=makeQuery(id+"F4.opExtrude","SWEPT_EDGE",EDGE,{"disambiguationData":[OSD([sQuery(id+"F3.wireOp",EDGE,"E26.MirrorCS"),sQuery(id+"F3.wireOp",EDGE,"E30.MirrorCS")])]});
            var Q6;
            Q6=makeQuery(id+"F4.opExtrude","SWEPT_EDGE",EDGE,{"disambiguationData":[OSD([sQuery(id+"F3.wireOp",EDGE,"E43.MirrorCS"),sQuery(id+"F3.wireOp",EDGE,"E40.MirrorCS")])]});
            var Q7;
            Q7=makeQuery(id+"F4.opExtrude","SWEPT_EDGE",EDGE,{"disambiguationData":[OSD([sQuery(id+"F3.wireOp",EDGE,"E38.MirrorCS"),sQuery(id+"F3.wireOp",EDGE,"E40.MirrorCS")])]});
            fillet(context, id + "F16", {"entities" : qUnion([Q0, Q1, Q2, Q3, Q4, Q5, Q6, Q7]), "radius" : 2 * mm, "tangentPropagation" : true, "allowEdgeOverflow" : false});
        }
        {
            var Q0;
            Q0=makeQuery(id+"F4.opExtrude","CAP_EDGE",EDGE,{"disambiguationData":[OSD([sQuery(id+"F3.wireOp",EDGE,"E35.MirrorCS")])],"isStart":false});
            var Q1;
            Q1=makeQuery(id+"F4.opExtrude","CAP_EDGE",EDGE,{"disambiguationData":[OSD([sQuery(id+"F3.wireOp",EDGE,"E36.MirrorCS")])],"isStart":false});
            var Q2;
            Q2=makeQuery(id+"F4.opExtrude","CAP_EDGE",EDGE,{"disambiguationData":[OSD([sQuery(id+"F3.wireOp",EDGE,"E20")])],"isStart":false});
            var Q3;
            Q3=makeQuery(id+"F4.opExtrude","CAP_EDGE",EDGE,{"disambiguationData":[OSD([sQuery(id+"F3.wireOp",EDGE,"E19")])],"isStart":false});
            var Q4;
            Q4=makeQuery(id+"F4.opExtrude","CAP_EDGE",EDGE,{"disambiguationData":[OSD([sQuery(id+"F3.wireOp",EDGE,"E23.MirrorCS")])],"isStart":false});
            var Q5;
            Q5=makeQuery(id+"F4.opExtrude","CAP_EDGE",EDGE,{"disambiguationData":[OSD([sQuery(id+"F3.wireOp",EDGE,"E24.MirrorCS")])],"isStart":false});
            var Q6;
            Q6=makeQuery(id+"F4.opExtrude","CAP_EDGE",EDGE,{"disambiguationData":[OSD([sQuery(id+"F3.wireOp",EDGE,"E34.MirrorCS")])],"isStart":false});
            var Q7;
            Q7=makeQuery(id+"F4.opExtrude","CAP_EDGE",EDGE,{"disambiguationData":[OSD([sQuery(id+"F3.wireOp",EDGE,"E33.MirrorCS")])],"isStart":false});
            var Q8;
            Q8=makeQuery(id+"F10.boolean.opBoolean","COPY",EDGE,{"derivedFrom":makeQuery(id+"F10.opExtrude","CAP_EDGE",EDGE,{"disambiguationData":[OSD([sQuery(id+"F9.wireOp",EDGE,"E53.top")])],"isStart":false})});
            var Q9;
            Q9=makeQuery(id+"F10.boolean.opBoolean","COPY",EDGE,{"derivedFrom":makeQuery(id+"F10.opExtrude","CAP_EDGE",EDGE,{"disambiguationData":[OSD([sQuery(id+"F9.wireOp",EDGE,"E53.bottom")])],"isStart":false})});
            var Q10;
            Q10=makeQuery(id+"F10.boolean.opBoolean","COPY",EDGE,{"derivedFrom":makeQuery(id+"F10.opExtrude","CAP_EDGE",EDGE,{"disambiguationData":[OSD([sQuery(id+"F9.wireOp",EDGE,"Me13D1SK-nVIm-EUZ4-u9ei-o20qw3bNrjn4.bottom")])],"isStart":false})});
            var Q11;
            Q11=makeQuery(id+"F10.boolean.opBoolean","COPY",EDGE,{"derivedFrom":makeQuery(id+"F10.opExtrude","CAP_EDGE",EDGE,{"disambiguationData":[OSD([sQuery(id+"F9.wireOp",EDGE,"Me13D1SK-nVIm-EUZ4-u9ei-o20qw3bNrjn4.top")])],"isStart":false})});
            var Q12;
            Q12=makeQuery(id+"F4.opExtrude","CAP_EDGE",EDGE,{"disambiguationData":[OSD([sQuery(id+"F3.wireOp",EDGE,"E36.MirrorCS")])],"isStart":true});
            var Q13;
            Q13=makeQuery(id+"F4.opExtrude","CAP_EDGE",EDGE,{"disambiguationData":[OSD([sQuery(id+"F3.wireOp",EDGE,"E20")])],"isStart":true});
            var Q14;
            Q14=makeQuery(id+"F4.opExtrude","CAP_EDGE",EDGE,{"disambiguationData":[OSD([sQuery(id+"F3.wireOp",EDGE,"E19")])],"isStart":true});
            var Q15;
            Q15=makeQuery(id+"F4.opExtrude","CAP_EDGE",EDGE,{"disambiguationData":[OSD([sQuery(id+"F3.wireOp",EDGE,"E23.MirrorCS")])],"isStart":true});
            var Q16;
            Q16=makeQuery(id+"F4.opExtrude","CAP_EDGE",EDGE,{"disambiguationData":[OSD([sQuery(id+"F3.wireOp",EDGE,"E35.MirrorCS")])],"isStart":true});
            var Q17;
            Q17=makeQuery(id+"F4.opExtrude","CAP_EDGE",EDGE,{"disambiguationData":[OSD([sQuery(id+"F3.wireOp",EDGE,"E33.MirrorCS")])],"isStart":true});
            var Q18;
            Q18=makeQuery(id+"F4.opExtrude","CAP_EDGE",EDGE,{"disambiguationData":[OSD([sQuery(id+"F3.wireOp",EDGE,"E34.MirrorCS")])],"isStart":true});
            var Q19;
            Q19=makeQuery(id+"F4.opExtrude","CAP_EDGE",EDGE,{"disambiguationData":[OSD([sQuery(id+"F3.wireOp",EDGE,"E24.MirrorCS")])],"isStart":true});
            fillet(context, id + "F17", {"entities" : qUnion([Q0, Q1, Q2, Q3, Q4, Q5, Q6, Q7, Q8, Q9, Q10, Q11, Q12, Q13, Q14, Q15, Q16, Q17, Q18, Q19]), "radius" : 1 * mm, "tangentPropagation" : true, "allowEdgeOverflow" : false});
        }
        {
            var Q0;
            Q0=makeQuery(id+"F1.opExtrude","CAP_EDGE",EDGE,{"disambiguationData":[OSD([sQuery(id+"F0.wireOp",EDGE,"E0.bottom")])],"isStart":false});
            fillet(context, id + "F18", {"entities" : qUnion([Q0]), "radius" : 1 * mm, "tangentPropagation" : true, "allowEdgeOverflow" : false});
        }
        {
            var Q0;
            {var subQ0=sQuery(id+"F3.wireOp",EDGE,"E28.MirrorCS");var subQ1=sQuery(id+"F3.wireOp",EDGE,"E15");var subQ2=sQuery(id+"F0.wireOp",EDGE,"E0.right");var subQ4=sQuery(id+"F3.wireOp",EDGE,"E29.MirrorCS");var subQ5=sQuery(id+"F0.wireOp",EDGE,"E6");var subQ7=makeQuery(id+"F8.opShell","OFFSET_EDGE",EDGE,{"disambiguationData":[OSD([subQ2,subQ5,subQ1,subQ0,subQ4])]});Q0=makeQuery(id+"F12.boolean.opBoolean","MERGE",EDGE,{"derivedFrom":[makeQuery(id+"F10.boolean.opBoolean","SPLIT",EDGE,{"disambiguationData":[TD([makeQuery(id+"F10.opExtrude","SWEPT_FACE",FACE,{"disambiguationData":[OSD([sQuery(id+"F9.wireOp",EDGE,"Me13D1SK-nVIm-EUZ4-u9ei-o20qw3bNrjn4.top")])]})])],"derivedFrom":subQ7}),makeQuery(id+"F10.boolean.opBoolean","SPLIT",EDGE,{"disambiguationData":[TD([makeQuery(id+"F10.opExtrude","SWEPT_FACE",FACE,{"disambiguationData":[OSD([sQuery(id+"F9.wireOp",EDGE,"E53.bottom")])]})])],"derivedFrom":subQ7}),makeQuery(id+"F10.boolean.opBoolean","SPLIT",EDGE,{"disambiguationData":[TD([makeQuery(id+"F10.opExtrude","SWEPT_FACE",FACE,{"disambiguationData":[OSD([sQuery(id+"F9.wireOp",EDGE,"Me13D1SK-nVIm-EUZ4-u9ei-o20qw3bNrjn4.bottom")])]})])],"derivedFrom":subQ7}),makeQuery(id+"F12.opExtrude","SWEPT_EDGE",EDGE,{"disambiguationData":[OSD([sQuery(id+"F11.wireOp",EDGE,"E55.8"),sQuery(id+"F11.wireOp",EDGE,"E56")])]})]});}
            var Q1;
            {var subQ0=sQuery(id+"F3.wireOp",EDGE,"E39.MirrorCS");var subQ1=sQuery(id+"F3.wireOp",EDGE,"E25.MirrorCS");var subQ2=sQuery(id+"F0.wireOp",EDGE,"E0.bottom");var subQ4=sQuery(id+"F3.wireOp",EDGE,"E29.MirrorCS");var subQ5=sQuery(id+"F0.wireOp",EDGE,"E6");var subQ7=makeQuery(id+"F8.opShell","OFFSET_EDGE",EDGE,{"disambiguationData":[OSD([subQ2,subQ5,subQ1,subQ4,subQ0])]});Q1=makeQuery(id+"F12.boolean.opBoolean","MERGE",EDGE,{"derivedFrom":[makeQuery(id+"F10.boolean.opBoolean","SPLIT",EDGE,{"disambiguationData":[TD([makeQuery(id+"F10.opExtrude","SWEPT_FACE",FACE,{"disambiguationData":[OSD([sQuery(id+"F9.wireOp",EDGE,"Me13D1SK-nVIm-EUZ4-u9ei-o20qw3bNrjn4.top")])]})])],"derivedFrom":subQ7}),makeQuery(id+"F10.boolean.opBoolean","SPLIT",EDGE,{"disambiguationData":[TD([makeQuery(id+"F10.opExtrude","SWEPT_FACE",FACE,{"disambiguationData":[OSD([sQuery(id+"F9.wireOp",EDGE,"E53.bottom")])]})])],"derivedFrom":subQ7}),makeQuery(id+"F10.boolean.opBoolean","SPLIT",EDGE,{"disambiguationData":[TD([makeQuery(id+"F10.opExtrude","SWEPT_FACE",FACE,{"disambiguationData":[OSD([sQuery(id+"F9.wireOp",EDGE,"Me13D1SK-nVIm-EUZ4-u9ei-o20qw3bNrjn4.bottom")])]})])],"derivedFrom":subQ7}),makeQuery(id+"F12.opExtrude","SWEPT_EDGE",EDGE,{"disambiguationData":[OSD([sQuery(id+"F11.wireOp",EDGE,"E55.4"),sQuery(id+"F11.wireOp",EDGE,"E56")])]})]});}
            var Q2;
            {var subQ0=sQuery(id+"F3.wireOp",EDGE,"E28.MirrorCS");var subQ1=sQuery(id+"F3.wireOp",EDGE,"E15");var subQ2=sQuery(id+"F0.wireOp",EDGE,"E0.right");var subQ4=sQuery(id+"F3.wireOp",EDGE,"E11");var subQ5=sQuery(id+"F0.wireOp",EDGE,"E5");var subQ7=makeQuery(id+"F8.opShell","OFFSET_EDGE",EDGE,{"disambiguationData":[OSD([subQ2,subQ5,subQ4,subQ1,subQ0])]});Q2=makeQuery(id+"F12.boolean.opBoolean","MERGE",EDGE,{"derivedFrom":[makeQuery(id+"F10.boolean.opBoolean","SPLIT",EDGE,{"disambiguationData":[TD([makeQuery(id+"F10.opExtrude","SWEPT_FACE",FACE,{"disambiguationData":[OSD([sQuery(id+"F9.wireOp",EDGE,"Me13D1SK-nVIm-EUZ4-u9ei-o20qw3bNrjn4.top")])]})])],"derivedFrom":subQ7}),makeQuery(id+"F10.boolean.opBoolean","SPLIT",EDGE,{"disambiguationData":[TD([makeQuery(id+"F10.opExtrude","SWEPT_FACE",FACE,{"disambiguationData":[OSD([sQuery(id+"F9.wireOp",EDGE,"E53.bottom")])]})])],"derivedFrom":subQ7}),makeQuery(id+"F10.boolean.opBoolean","SPLIT",EDGE,{"disambiguationData":[TD([makeQuery(id+"F10.opExtrude","SWEPT_FACE",FACE,{"disambiguationData":[OSD([sQuery(id+"F9.wireOp",EDGE,"Me13D1SK-nVIm-EUZ4-u9ei-o20qw3bNrjn4.bottom")])]})])],"derivedFrom":subQ7}),makeQuery(id+"F12.opExtrude","SWEPT_EDGE",EDGE,{"disambiguationData":[OSD([sQuery(id+"F11.wireOp",EDGE,"E55.8"),sQuery(id+"F11.wireOp",EDGE,"E59")])]})]});}
            var Q3;
            {var subQ0=sQuery(id+"F3.wireOp",EDGE,"E37.MirrorCS");var subQ1=sQuery(id+"F3.wireOp",EDGE,"E16");var subQ2=sQuery(id+"F0.wireOp",EDGE,"E0.top");var subQ4=sQuery(id+"F3.wireOp",EDGE,"E11");var subQ5=sQuery(id+"F0.wireOp",EDGE,"E5");var subQ7=makeQuery(id+"F8.opShell","OFFSET_EDGE",EDGE,{"disambiguationData":[OSD([subQ2,subQ5,subQ4,subQ1,subQ0])]});Q3=makeQuery(id+"F12.boolean.opBoolean","MERGE",EDGE,{"derivedFrom":[makeQuery(id+"F10.boolean.opBoolean","SPLIT",EDGE,{"disambiguationData":[TD([makeQuery(id+"F10.opExtrude","SWEPT_FACE",FACE,{"disambiguationData":[OSD([sQuery(id+"F9.wireOp",EDGE,"Me13D1SK-nVIm-EUZ4-u9ei-o20qw3bNrjn4.top")])]})])],"derivedFrom":subQ7}),makeQuery(id+"F10.boolean.opBoolean","SPLIT",EDGE,{"disambiguationData":[TD([makeQuery(id+"F10.opExtrude","SWEPT_FACE",FACE,{"disambiguationData":[OSD([sQuery(id+"F9.wireOp",EDGE,"E53.bottom")])]})])],"derivedFrom":subQ7}),makeQuery(id+"F10.boolean.opBoolean","SPLIT",EDGE,{"disambiguationData":[TD([makeQuery(id+"F10.opExtrude","SWEPT_FACE",FACE,{"disambiguationData":[OSD([sQuery(id+"F9.wireOp",EDGE,"Me13D1SK-nVIm-EUZ4-u9ei-o20qw3bNrjn4.bottom")])]})])],"derivedFrom":subQ7}),makeQuery(id+"F12.opExtrude","SWEPT_EDGE",EDGE,{"disambiguationData":[OSD([sQuery(id+"F11.wireOp",EDGE,"E55.12"),sQuery(id+"F11.wireOp",EDGE,"E59")])]})]});}
            var Q4;
            {var subQ0=sQuery(id+"F3.wireOp",EDGE,"E37.MirrorCS");var subQ1=sQuery(id+"F3.wireOp",EDGE,"E16");var subQ2=sQuery(id+"F0.wireOp",EDGE,"E0.top");var subQ4=sQuery(id+"F3.wireOp",EDGE,"E49.MirrorCS");var subQ5=sQuery(id+"F0.wireOp",EDGE,"E4");var subQ7=makeQuery(id+"F8.opShell","OFFSET_EDGE",EDGE,{"disambiguationData":[OSD([subQ2,subQ5,subQ1,subQ0,subQ4])]});Q4=makeQuery(id+"F12.boolean.opBoolean","MERGE",EDGE,{"derivedFrom":[makeQuery(id+"F10.boolean.opBoolean","SPLIT",EDGE,{"disambiguationData":[TD([makeQuery(id+"F10.opExtrude","SWEPT_FACE",FACE,{"disambiguationData":[OSD([sQuery(id+"F9.wireOp",EDGE,"Me13D1SK-nVIm-EUZ4-u9ei-o20qw3bNrjn4.top")])]})])],"derivedFrom":subQ7}),makeQuery(id+"F10.boolean.opBoolean","SPLIT",EDGE,{"disambiguationData":[TD([makeQuery(id+"F10.opExtrude","SWEPT_FACE",FACE,{"disambiguationData":[OSD([sQuery(id+"F9.wireOp",EDGE,"E53.bottom")])]})])],"derivedFrom":subQ7}),makeQuery(id+"F10.boolean.opBoolean","SPLIT",EDGE,{"disambiguationData":[TD([makeQuery(id+"F10.opExtrude","SWEPT_FACE",FACE,{"disambiguationData":[OSD([sQuery(id+"F9.wireOp",EDGE,"Me13D1SK-nVIm-EUZ4-u9ei-o20qw3bNrjn4.bottom")])]})])],"derivedFrom":subQ7}),makeQuery(id+"F12.opExtrude","SWEPT_EDGE",EDGE,{"disambiguationData":[OSD([sQuery(id+"F11.wireOp",EDGE,"E55.12"),sQuery(id+"F11.wireOp",EDGE,"E58")])]})]});}
            var Q5;
            {var subQ0=sQuery(id+"F3.wireOp",EDGE,"E44.MirrorCS");var subQ1=sQuery(id+"F3.wireOp",EDGE,"E45.MirrorCS");var subQ2=sQuery(id+"F0.wireOp",EDGE,"E0.left");var subQ4=sQuery(id+"F3.wireOp",EDGE,"E49.MirrorCS");var subQ5=sQuery(id+"F0.wireOp",EDGE,"E4");var subQ7=makeQuery(id+"F8.opShell","OFFSET_EDGE",EDGE,{"disambiguationData":[OSD([subQ2,subQ5,subQ1,subQ0,subQ4])]});Q5=makeQuery(id+"F12.boolean.opBoolean","MERGE",EDGE,{"derivedFrom":[makeQuery(id+"F10.boolean.opBoolean","SPLIT",EDGE,{"disambiguationData":[TD([makeQuery(id+"F10.opExtrude","SWEPT_FACE",FACE,{"disambiguationData":[OSD([sQuery(id+"F9.wireOp",EDGE,"Me13D1SK-nVIm-EUZ4-u9ei-o20qw3bNrjn4.top")])]})])],"derivedFrom":subQ7}),makeQuery(id+"F10.boolean.opBoolean","SPLIT",EDGE,{"disambiguationData":[TD([makeQuery(id+"F10.opExtrude","SWEPT_FACE",FACE,{"disambiguationData":[OSD([sQuery(id+"F9.wireOp",EDGE,"E53.bottom")])]})])],"derivedFrom":subQ7}),makeQuery(id+"F10.boolean.opBoolean","SPLIT",EDGE,{"disambiguationData":[TD([makeQuery(id+"F10.opExtrude","SWEPT_FACE",FACE,{"disambiguationData":[OSD([sQuery(id+"F9.wireOp",EDGE,"Me13D1SK-nVIm-EUZ4-u9ei-o20qw3bNrjn4.bottom")])]})])],"derivedFrom":subQ7}),makeQuery(id+"F12.opExtrude","SWEPT_EDGE",EDGE,{"disambiguationData":[OSD([sQuery(id+"F11.wireOp",EDGE,"E55.2"),sQuery(id+"F11.wireOp",EDGE,"E58")])]})]});}
            var Q6;
            {var subQ0=sQuery(id+"F3.wireOp",EDGE,"E44.MirrorCS");var subQ1=sQuery(id+"F3.wireOp",EDGE,"E45.MirrorCS");var subQ2=sQuery(id+"F0.wireOp",EDGE,"E0.left");var subQ4=sQuery(id+"F3.wireOp",EDGE,"E42.MirrorCS");var subQ5=sQuery(id+"F0.wireOp",EDGE,"E3");var subQ7=makeQuery(id+"F8.opShell","OFFSET_EDGE",EDGE,{"disambiguationData":[OSD([subQ2,subQ5,subQ1,subQ0,subQ4])]});Q6=makeQuery(id+"F12.boolean.opBoolean","MERGE",EDGE,{"derivedFrom":[makeQuery(id+"F10.boolean.opBoolean","SPLIT",EDGE,{"disambiguationData":[TD([makeQuery(id+"F10.opExtrude","SWEPT_FACE",FACE,{"disambiguationData":[OSD([sQuery(id+"F9.wireOp",EDGE,"Me13D1SK-nVIm-EUZ4-u9ei-o20qw3bNrjn4.top")])]})])],"derivedFrom":subQ7}),makeQuery(id+"F10.boolean.opBoolean","SPLIT",EDGE,{"disambiguationData":[TD([makeQuery(id+"F10.opExtrude","SWEPT_FACE",FACE,{"disambiguationData":[OSD([sQuery(id+"F9.wireOp",EDGE,"E53.bottom")])]})])],"derivedFrom":subQ7}),makeQuery(id+"F10.boolean.opBoolean","SPLIT",EDGE,{"disambiguationData":[TD([makeQuery(id+"F10.opExtrude","SWEPT_FACE",FACE,{"disambiguationData":[OSD([sQuery(id+"F9.wireOp",EDGE,"Me13D1SK-nVIm-EUZ4-u9ei-o20qw3bNrjn4.bottom")])]})])],"derivedFrom":subQ7}),makeQuery(id+"F12.opExtrude","SWEPT_EDGE",EDGE,{"disambiguationData":[OSD([sQuery(id+"F11.wireOp",EDGE,"E55.2"),sQuery(id+"F11.wireOp",EDGE,"E57")])]})]});}
            var Q7;
            {var subQ0=sQuery(id+"F3.wireOp",EDGE,"E39.MirrorCS");var subQ1=sQuery(id+"F3.wireOp",EDGE,"E25.MirrorCS");var subQ2=sQuery(id+"F0.wireOp",EDGE,"E0.bottom");var subQ4=sQuery(id+"F3.wireOp",EDGE,"E42.MirrorCS");var subQ5=sQuery(id+"F0.wireOp",EDGE,"E3");var subQ7=makeQuery(id+"F8.opShell","OFFSET_EDGE",EDGE,{"disambiguationData":[OSD([subQ2,subQ5,subQ1,subQ0,subQ4])]});Q7=makeQuery(id+"F12.boolean.opBoolean","MERGE",EDGE,{"derivedFrom":[makeQuery(id+"F10.boolean.opBoolean","SPLIT",EDGE,{"disambiguationData":[TD([makeQuery(id+"F10.opExtrude","SWEPT_FACE",FACE,{"disambiguationData":[OSD([sQuery(id+"F9.wireOp",EDGE,"Me13D1SK-nVIm-EUZ4-u9ei-o20qw3bNrjn4.top")])]})])],"derivedFrom":subQ7}),makeQuery(id+"F10.boolean.opBoolean","SPLIT",EDGE,{"disambiguationData":[TD([makeQuery(id+"F10.opExtrude","SWEPT_FACE",FACE,{"disambiguationData":[OSD([sQuery(id+"F9.wireOp",EDGE,"E53.bottom")])]})])],"derivedFrom":subQ7}),makeQuery(id+"F10.boolean.opBoolean","SPLIT",EDGE,{"disambiguationData":[TD([makeQuery(id+"F10.opExtrude","SWEPT_FACE",FACE,{"disambiguationData":[OSD([sQuery(id+"F9.wireOp",EDGE,"Me13D1SK-nVIm-EUZ4-u9ei-o20qw3bNrjn4.bottom")])]})])],"derivedFrom":subQ7}),makeQuery(id+"F12.opExtrude","SWEPT_EDGE",EDGE,{"disambiguationData":[OSD([sQuery(id+"F11.wireOp",EDGE,"E55.4"),sQuery(id+"F11.wireOp",EDGE,"E57")])]})]});}
            fillet(context, id + "F19", {"entities" : qUnion([Q0, Q1, Q2, Q3, Q4, Q5, Q6, Q7]), "radius" : 1 * mm, "tangentPropagation" : true, "allowEdgeOverflow" : false});
        }
    });
